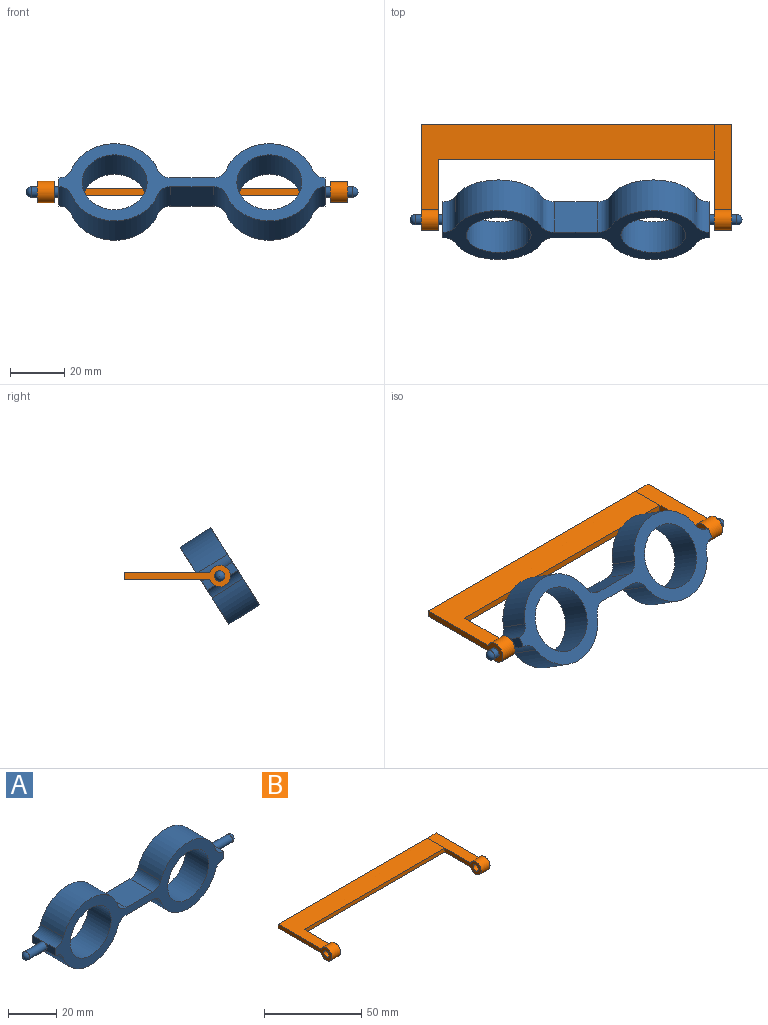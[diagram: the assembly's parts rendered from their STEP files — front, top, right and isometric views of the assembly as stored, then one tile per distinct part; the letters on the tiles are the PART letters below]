
ASSEMBLY  parts=2 mates=1
PART A: 26 faces, bbox 122.7x13.4x33.7 mm
  f0: plane 6.7x3.79mm, normal (1,0,0), area 19.8mm2, adj f9,f11,f21,f25
  f1: plane 6.7x3.79mm, normal (-1,0,0), area 19.8mm2, adj f3,f19,f21,f22
  f2: plane 6.7x3.79mm, normal (-1,0,0), area 19.8mm2, adj f3,f19,f20,f22
  f3: cylinder r=5mm len=13.4mm, axis (0,1,0), area 83.7mm2, adj f1,f2,f4,f20,f21
  f4: cylinder r=16.86mm len=32mm, axis (0,1,0), area 564.8mm2, adj f3,f5,f20,f21
  f5: cylinder r=5mm len=13.4mm, axis (0,1,0), area 83.7mm2, adj f4,f6,f20,f21
  f6: plane 15.68x13.4mm, normal (0,0,-1), area 210.1mm2, adj f5,f7,f20,f21
  f7: cylinder r=5mm len=13.4mm, axis (0,1,0), area 83.7mm2, adj f6,f8,f20,f21
  f8: cylinder r=16.86mm len=32mm, axis (0,1,0), area 564.8mm2, adj f7,f9,f20,f21
  f9: cylinder r=5mm len=13.4mm, axis (0,1,0), area 83.7mm2, adj f0,f8,f10,f20,f21
  f10: plane 6.7x3.79mm, normal (1,0,0), area 19.8mm2, adj f9,f11,f20,f25
  f11: cylinder r=5mm len=13.4mm, axis (0,1,0), area 83.7mm2, adj f0,f10,f12,f20,f21
  f12: cylinder r=16.86mm len=32mm, axis (0,1,0), area 564.8mm2, adj f11,f13,f20,f21
  f13: cylinder r=5mm len=13.4mm, axis (0,1,0), area 83.7mm2, adj f12,f14,f20,f21
  f14: plane 15.68x13.4mm, normal (0,0,1), area 210.1mm2, adj f13,f15,f20,f21
  f15: cylinder r=5mm len=13.4mm, axis (0,1,0), area 83.7mm2, adj f14,f16,f20,f21
  f16: cylinder r=16.86mm len=32mm, axis (0,1,0), area 564.8mm2, adj f15,f19,f20,f21
  f17: cylinder r=11.99mm len=23.99mm, axis (0,1,0), area 1009.8mm2, adj f20,f21
  f18: cylinder r=11.99mm len=23.99mm, axis (0,1,0), area 1009.8mm2, adj f20,f21
  f19: cylinder r=5mm len=13.4mm, axis (0,1,0), area 83.7mm2, adj f1,f2,f16,f20,f21
  f20: plane 98.66x33.72mm, normal (0,-1,0), area 1024.2mm2, adj f2,f3,f4,f5,f6,f7,f8,f9
  f21: plane 98.66x33.72mm, normal (0,1,0), area 1024.2mm2, adj f0,f1,f3,f4,f5,f6,f7,f8
  f22: cylinder r=1.9mm len=10.13mm, axis (-1,0,0), area 120.7mm2, adj f1,f2,f23
  f23: sphere r=1.9mm, area 22.6mm2, adj f22
  f24: sphere r=1.9mm, area 22.6mm2, adj f25
  f25: cylinder r=1.9mm len=10.13mm, axis (-1,0,0), area 120.7mm2, adj f0,f10,f24
PART B: 17 faces, bbox 114.9x39.1x7.9 mm
  f0: plane 102.1x2.46mm, normal (0,-1,0), area 250.4mm2, adj f1,f10,f11,f13
  f1: plane 39x7.74mm, normal (-1,0,0), area 82.2mm2, adj f0,f2,f3,f4,f5,f6,f11
  f2: plane 31.47x6.5mm, normal (0,0,-1), area 204.5mm2, adj f1,f3,f6,f7
  f3: plane 6.5x2.49mm, normal (0,1,0), area 16.2mm2, adj f1,f2,f4,f7,f8
  f4: plane 31.48x6.52mm, normal (0,0,1), area 204.5mm2, adj f1,f3,f6,f7,f10
  f5: cylinder r=1.9mm len=6.5mm, axis (-1,0,0), area 77.4mm2, adj f1,f7
  f6: cylinder r=3.87mm len=7.74mm, axis (-1,0,0), area 141.7mm2, adj f1,f2,f4,f7
  f7: plane 39x7.74mm, normal (1,0,0), area 113.7mm2, adj f2,f3,f4,f5,f6
  f8: plane 2.46x0.05mm, normal (1,0,0), area 0.1mm2, adj f3,f9,f10,f11
  f9: plane 108.4x2.45mm, normal (0,1,0), area 265.9mm2, adj f8,f10,f11,f12
  f10: plane 108.42x31.44mm, normal (0,0,1), area 1503.5mm2, adj f0,f4,f8,f9,f12,f13,f15
  f11: plane 108.4x31.42mm, normal (0,0,-1), area 1503.5mm2, adj f0,f1,f8,f9,f12,f13,f14
  f12: plane 39.12x7.89mm, normal (-1,0,0), area 114.4mm2, adj f9,f10,f11,f14,f15,f16
  f13: plane 26.33x7.89mm, normal (1,0,0), area 83mm2, adj f0,f10,f11,f14,f15,f16
  f14: cylinder r=3.94mm len=7.89mm, axis (-1,0,0), area 140.5mm2, adj f11,f12,f13,f15
  f15: plane 6.3x0.02mm, normal (0,-1,0), area 0.1mm2, adj f10,f12,f13,f14
  f16: cylinder r=1.9mm len=6.3mm, axis (-1,0,0), area 75mm2, adj f12,f13
PLACE A rot(axis=(-1,0,0),32.4deg) t=(-9.22,17.04,7.94)mm
PLACE B t=(41.92,23.19,7.94)mm fixed
MATE revolute A.f25 <-> B.f5  axis (-1,0,0) through (45.17,17.04,7.94)mm
